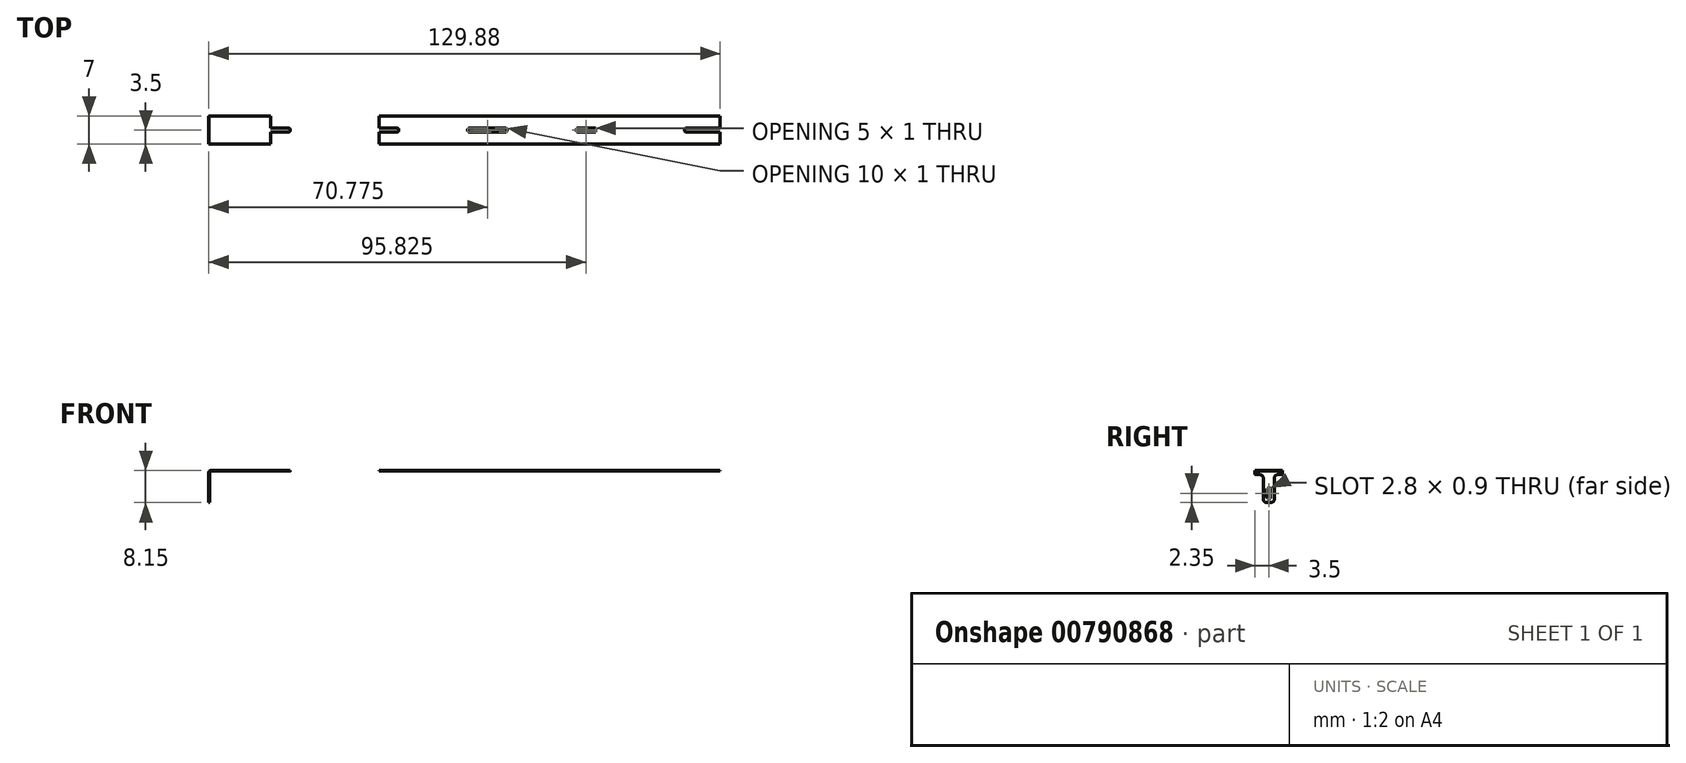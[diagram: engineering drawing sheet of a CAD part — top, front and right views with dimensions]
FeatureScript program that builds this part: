
annotation { "Feature Type Name" : "Feature", "Feature Type Description" : "" }
export const myFeature = defineFeature(function(context is Context, id is Id, definition is map)
    precondition{}
    {
        {
            var Q0;
            Q0=qCreatedBy(makeId("Top.planeOp"),FACE);
            var sketch = newSketch(context, id + "F0", { "sketchPlane" : qUnion([Q0])});
            skPoint(sketch, "E0.middle", {"position": v(0, 0) * mm});
            skLineSegment(sketch, "E1.bottom", {"start": v(-9.18, -0.5) * mm, "end": v(-13.77, -0.5) * mm});
            skLineSegment(sketch, "E1.top", {"start": v(-9.18, 0.5) * mm, "end": v(-13.77, 0.5) * mm});
            skLineSegment(sketch, "E1.left", {"start": v(-8.78, -0.1) * mm, "end": v(-8.78, 0.1) * mm});
            skLineSegment(sketch, "E1.right", {"start": v(-18.78, -0.1) * mm, "end": v(-18.78, 0.1) * mm});
            skPoint(sketch, "E1.middle", {"position": v(-13.78, 0) * mm});
            skPoint(sketch, "E2.visualSharp", {"position": v(-8.78, 0.5) * mm});
            skArc(sketch, "E2.filletArc", {"start": v(-8.78, 0.1) * mm, "mid": v(-8.9, 0.38) * mm, "end": v(-9.18, 0.5) * mm});
            skPoint(sketch, "E3.visualSharp", {"position": v(-8.78, -0.5) * mm});
            skArc(sketch, "E3.filletArc", {"start": v(-9.18, -0.5) * mm, "mid": v(-8.9, -0.38) * mm, "end": v(-8.78, -0.1) * mm});
            skPoint(sketch, "E4.visualSharp", {"position": v(-18.78, 0.5) * mm});
            skArc(sketch, "E4.filletArc", {"start": v(-18.38, 0.5) * mm, "mid": v(-18.66, 0.38) * mm, "end": v(-18.77, 0.1) * mm});
            skPoint(sketch, "E5.visualSharp", {"position": v(-18.78, -0.5) * mm});
            skArc(sketch, "E5.filletArc", {"start": v(-18.77, -0.1) * mm, "mid": v(-18.66, -0.38) * mm, "end": v(-18.38, -0.5) * mm});
            skLineSegment(sketch, "E6", {"start": v(0, 3.5) * mm, "end": v(-13.78, 3.5) * mm});
            skPoint(sketch, "E6.endSnap0", {"position": v(-13.77, 0.5) * mm});
            skLineSegment(sketch, "E7", {"start": v(-13.78, 3.5) * mm, "end": v(-13.78, 0.5) * mm});
            skLineSegment(sketch, "E8.MirrorCS", {"start": v(0, -3.5) * mm, "end": v(-13.78, -3.5) * mm});
            skLineSegment(sketch, "E9.MirrorCS", {"start": v(-13.78, -3.5) * mm, "end": v(-13.78, -0.5) * mm});
            skLineSegment(sketch, "E10.MirrorCS", {"start": v(0, 3.5) * mm, "end": v(13.78, 3.5) * mm});
            skLineSegment(sketch, "E11.MirrorCS", {"start": v(0, -3.5) * mm, "end": v(13.78, -3.5) * mm});
            skLineSegment(sketch, "E12.MirrorCS", {"start": v(8.78, -0.1) * mm, "end": v(8.78, 0.1) * mm});
            skArc(sketch, "E13.MirrorCS", {"start": v(8.78, 0.1) * mm, "mid": v(8.9, 0.38) * mm, "end": v(9.18, 0.5) * mm});
            skArc(sketch, "E14.MirrorCS", {"start": v(18.77, -0.1) * mm, "mid": v(18.66, -0.38) * mm, "end": v(18.38, -0.5) * mm});
            skLineSegment(sketch, "E15.MirrorCS", {"start": v(18.78, -0.1) * mm, "end": v(18.78, 0.1) * mm});
            skArc(sketch, "E16.MirrorCS", {"start": v(18.38, 0.5) * mm, "mid": v(18.66, 0.38) * mm, "end": v(18.77, 0.1) * mm});
            skArc(sketch, "E17.MirrorCS", {"start": v(9.18, -0.5) * mm, "mid": v(8.9, -0.38) * mm, "end": v(8.78, -0.1) * mm});
            skPoint(sketch, "E18.MirrorP", {"position": v(18.78, 0.5) * mm});
            skLineSegment(sketch, "E19.MirrorCS", {"start": v(9.18, 0.5) * mm, "end": v(18.38, 0.5) * mm});
            skLineSegment(sketch, "E20.MirrorCS", {"start": v(9.18, -0.5) * mm, "end": v(18.38, -0.5) * mm});
            skPoint(sketch, "E21.MirrorP", {"position": v(13.77, 0.5) * mm});
            skPoint(sketch, "E22.MirrorP", {"position": v(8.78, 0.5) * mm});
            skPoint(sketch, "E23.MirrorP", {"position": v(18.78, -0.5) * mm});
            skPoint(sketch, "E24.MirrorP", {"position": v(8.78, -0.5) * mm});
            skPoint(sketch, "E25.MirrorP", {"position": v(13.78, 0) * mm});
            skLineSegment(sketch, "E26.MirrorCS", {"start": v(13.78, 3.5) * mm, "end": v(13.78, 0.5) * mm});
            skLineSegment(sketch, "E27.MirrorCS", {"start": v(13.78, -3.5) * mm, "end": v(13.78, -0.5) * mm});
            skPoint(sketch, "E28.1.0.0", {"position": v(36.33, 0.5) * mm});
            skLineSegment(sketch, "E28.1.0.1", {"start": v(27.55, 3.5) * mm, "end": v(41.33, 3.5) * mm});
            skLineSegment(sketch, "E28.1.0.2", {"start": v(36.73, -0.5) * mm, "end": v(45.93, -0.5) * mm});
            skPoint(sketch, "E28.1.0.3", {"position": v(27.55, 0) * mm});
            skLineSegment(sketch, "E28.1.0.4", {"start": v(27.55, -3.5) * mm, "end": v(41.33, -3.5) * mm});
            skPoint(sketch, "E28.1.0.5", {"position": v(41.33, 0.5) * mm});
            skPoint(sketch, "E28.1.0.6", {"position": v(41.33, 0) * mm});
            skPoint(sketch, "E28.1.0.7", {"position": v(46.33, -0.5) * mm});
            skPoint(sketch, "E28.1.0.8", {"position": v(36.33, -0.5) * mm});
            skLineSegment(sketch, "E28.1.0.9", {"start": v(27.55, -3.5) * mm, "end": v(13.78, -3.5) * mm});
            skLineSegment(sketch, "E28.1.0.10", {"start": v(36.73, 0.5) * mm, "end": v(45.93, 0.5) * mm});
            skLineSegment(sketch, "E28.1.0.11", {"start": v(27.55, 3.5) * mm, "end": v(13.78, 3.5) * mm});
            skLineSegment(sketch, "E28.1.0.12", {"start": v(41.33, 3.5) * mm, "end": v(41.33, 0.5) * mm});
            skLineSegment(sketch, "E28.1.0.13", {"start": v(41.33, -3.5) * mm, "end": v(41.33, -0.5) * mm});
            skPoint(sketch, "E28.1.0.14", {"position": v(46.33, 0.5) * mm});
            skArc(sketch, "E28.1.0.15", {"start": v(45.93, 0.5) * mm, "mid": v(46.2, 0.38) * mm, "end": v(46.32, 0.1) * mm});
            skArc(sketch, "E28.1.0.16", {"start": v(36.73, -0.5) * mm, "mid": v(36.44, -0.38) * mm, "end": v(36.33, -0.1) * mm});
            skArc(sketch, "E28.1.0.17", {"start": v(46.33, -0.1) * mm, "mid": v(46.2, -0.38) * mm, "end": v(45.93, -0.5) * mm});
            skArc(sketch, "E28.1.0.18", {"start": v(36.33, 0.1) * mm, "mid": v(36.44, 0.38) * mm, "end": v(36.73, 0.5) * mm});
            skLineSegment(sketch, "E28.1.0.19", {"start": v(36.32, -0.1) * mm, "end": v(36.32, 0.1) * mm});
            skLineSegment(sketch, "E28.1.0.20", {"start": v(46.33, -0.1) * mm, "end": v(46.33, 0.1) * mm});
            skPoint(sketch, "E28.2.0.0", {"position": v(63.88, 0.5) * mm});
            skLineSegment(sketch, "E28.2.0.1", {"start": v(55.1, 3.5) * mm, "end": v(68.88, 3.5) * mm});
            skLineSegment(sketch, "E28.2.0.2", {"start": v(64.28, -0.5) * mm, "end": v(73.48, -0.5) * mm});
            skPoint(sketch, "E28.2.0.3", {"position": v(55.1, 0) * mm});
            skLineSegment(sketch, "E28.2.0.4", {"start": v(55.1, -3.5) * mm, "end": v(68.88, -3.5) * mm});
            skPoint(sketch, "E28.2.0.5", {"position": v(68.88, 0.5) * mm});
            skPoint(sketch, "E28.2.0.6", {"position": v(68.88, 0) * mm});
            skPoint(sketch, "E28.2.0.7", {"position": v(73.88, -0.5) * mm});
            skPoint(sketch, "E28.2.0.8", {"position": v(63.88, -0.5) * mm});
            skLineSegment(sketch, "E28.2.0.9", {"start": v(55.1, -3.5) * mm, "end": v(41.33, -3.5) * mm});
            skLineSegment(sketch, "E28.2.0.10", {"start": v(64.28, 0.5) * mm, "end": v(73.48, 0.5) * mm});
            skLineSegment(sketch, "E28.2.0.11", {"start": v(55.1, 3.5) * mm, "end": v(41.33, 3.5) * mm});
            skLineSegment(sketch, "E28.2.0.12", {"start": v(68.88, 3.5) * mm, "end": v(68.88, 0.5) * mm});
            skLineSegment(sketch, "E28.2.0.13", {"start": v(68.88, -3.5) * mm, "end": v(68.88, -0.5) * mm});
            skPoint(sketch, "E28.2.0.14", {"position": v(73.88, 0.5) * mm});
            skArc(sketch, "E28.2.0.15", {"start": v(73.48, 0.5) * mm, "mid": v(73.76, 0.38) * mm, "end": v(73.88, 0.1) * mm});
            skArc(sketch, "E28.2.0.16", {"start": v(64.28, -0.5) * mm, "mid": v(64, -0.38) * mm, "end": v(63.88, -0.1) * mm});
            skArc(sketch, "E28.2.0.17", {"start": v(73.88, -0.1) * mm, "mid": v(73.76, -0.38) * mm, "end": v(73.48, -0.5) * mm});
            skArc(sketch, "E28.2.0.18", {"start": v(63.88, 0.1) * mm, "mid": v(64, 0.38) * mm, "end": v(64.28, 0.5) * mm});
            skLineSegment(sketch, "E28.2.0.19", {"start": v(63.88, -0.1) * mm, "end": v(63.88, 0.1) * mm});
            skLineSegment(sketch, "E28.2.0.20", {"start": v(73.88, -0.1) * mm, "end": v(73.88, 0.1) * mm});
            skPoint(sketch, "E28.3.0.0", {"position": v(91.43, 0.5) * mm});
            skLineSegment(sketch, "E28.3.0.1", {"start": v(82.65, 3.5) * mm, "end": v(96.43, 3.5) * mm});
            skLineSegment(sketch, "E28.3.0.2", {"start": v(91.83, -0.5) * mm, "end": v(101.03, -0.5) * mm});
            skPoint(sketch, "E28.3.0.3", {"position": v(82.65, 0) * mm});
            skLineSegment(sketch, "E28.3.0.4", {"start": v(82.65, -3.5) * mm, "end": v(96.43, -3.5) * mm});
            skPoint(sketch, "E28.3.0.5", {"position": v(96.43, 0.5) * mm});
            skPoint(sketch, "E28.3.0.6", {"position": v(96.42, 0) * mm});
            skPoint(sketch, "E28.3.0.7", {"position": v(101.42, -0.5) * mm});
            skPoint(sketch, "E28.3.0.8", {"position": v(91.43, -0.5) * mm});
            skLineSegment(sketch, "E28.3.0.9", {"start": v(82.65, -3.5) * mm, "end": v(68.88, -3.5) * mm});
            skLineSegment(sketch, "E28.3.0.10", {"start": v(91.83, 0.5) * mm, "end": v(101.03, 0.5) * mm});
            skLineSegment(sketch, "E28.3.0.11", {"start": v(82.65, 3.5) * mm, "end": v(68.88, 3.5) * mm});
            skLineSegment(sketch, "E28.3.0.12", {"start": v(96.43, 3.5) * mm, "end": v(96.43, 0.5) * mm});
            skLineSegment(sketch, "E28.3.0.13", {"start": v(96.43, -3.5) * mm, "end": v(96.43, -0.5) * mm});
            skPoint(sketch, "E28.3.0.14", {"position": v(101.42, 0.5) * mm});
            skArc(sketch, "E28.3.0.15", {"start": v(101.03, 0.5) * mm, "mid": v(101.3, 0.38) * mm, "end": v(101.42, 0.1) * mm});
            skArc(sketch, "E28.3.0.16", {"start": v(91.83, -0.5) * mm, "mid": v(91.54, -0.38) * mm, "end": v(91.43, -0.1) * mm});
            skArc(sketch, "E28.3.0.17", {"start": v(101.42, -0.1) * mm, "mid": v(101.3, -0.38) * mm, "end": v(101.03, -0.5) * mm});
            skArc(sketch, "E28.3.0.18", {"start": v(91.43, 0.1) * mm, "mid": v(91.54, 0.38) * mm, "end": v(91.83, 0.5) * mm});
            skLineSegment(sketch, "E28.3.0.19", {"start": v(91.43, -0.1) * mm, "end": v(91.43, 0.1) * mm});
            skLineSegment(sketch, "E28.3.0.20", {"start": v(101.42, -0.1) * mm, "end": v(101.42, 0.1) * mm});
            skLineSegment(sketch, "E28.direction1", {"start": v(-13.78, -3.5) * mm, "end": v(13.78, -3.5) * mm, "construction": true});
            skLineSegment(sketch, "E29", {"start": v(0, 3.5) * mm, "end": v(0, -3.5) * mm});
            skLineSegment(sketch, "E30.bottom", {"start": v(96.43, -3.5) * mm, "end": v(100.42, -3.5) * mm});
            skLineSegment(sketch, "E30.top", {"start": v(96.43, 3.5) * mm, "end": v(100.42, 3.5) * mm});
            skLineSegment(sketch, "E30.left", {"start": v(96.43, -3.5) * mm, "end": v(96.43, 3.5) * mm});
            skPoint(sketch, "E31.0.4.0", {"position": v(118.98, 0.5) * mm});
            skLineSegment(sketch, "E31.1.4.0", {"start": v(110.2, 3.5) * mm, "end": v(123.98, 3.5) * mm});
            skLineSegment(sketch, "E31.4.4.0", {"start": v(119.38, -0.5) * mm, "end": v(128.57, -0.5) * mm});
            skPoint(sketch, "E31.7.4.0", {"position": v(110.2, 0) * mm});
            skLineSegment(sketch, "E31.8.4.0", {"start": v(110.2, -3.5) * mm, "end": v(123.98, -3.5) * mm});
            skPoint(sketch, "E31.11.4.0", {"position": v(123.98, 0.5) * mm});
            skPoint(sketch, "E31.12.4.0", {"position": v(123.98, 0) * mm});
            skPoint(sketch, "E31.13.4.0", {"position": v(128.97, -0.5) * mm});
            skPoint(sketch, "E31.14.4.0", {"position": v(118.98, -0.5) * mm});
            skLineSegment(sketch, "E31.15.4.0", {"start": v(110.2, -3.5) * mm, "end": v(96.43, -3.5) * mm});
            skLineSegment(sketch, "E31.18.4.0", {"start": v(119.38, 0.5) * mm, "end": v(128.57, 0.5) * mm});
            skLineSegment(sketch, "E31.21.4.0", {"start": v(110.2, 3.5) * mm, "end": v(96.43, 3.5) * mm});
            skLineSegment(sketch, "E31.24.4.0", {"start": v(123.98, 3.5) * mm, "end": v(123.98, 0.5) * mm});
            skLineSegment(sketch, "E31.27.4.0", {"start": v(123.98, -3.5) * mm, "end": v(123.98, -0.5) * mm});
            skPoint(sketch, "E31.30.4.0", {"position": v(128.97, 0.5) * mm});
            skArc(sketch, "E31.31.4.0", {"start": v(128.57, 0.5) * mm, "mid": v(128.86, 0.38) * mm, "end": v(128.97, 0.1) * mm});
            skArc(sketch, "E31.35.4.0", {"start": v(119.38, -0.5) * mm, "mid": v(119.1, -0.38) * mm, "end": v(118.98, -0.1) * mm});
            skArc(sketch, "E31.39.4.0", {"start": v(128.97, -0.1) * mm, "mid": v(128.86, -0.38) * mm, "end": v(128.57, -0.5) * mm});
            skArc(sketch, "E31.43.4.0", {"start": v(118.98, 0.1) * mm, "mid": v(119.1, 0.38) * mm, "end": v(119.38, 0.5) * mm});
            skLineSegment(sketch, "E31.47.4.0", {"start": v(118.98, -0.1) * mm, "end": v(118.98, 0.1) * mm});
            skLineSegment(sketch, "E31.50.4.0", {"start": v(128.97, -0.1) * mm, "end": v(128.97, 0.1) * mm});
            skLineSegment(sketch, "E32.bottom", {"start": v(123.98, -3.5) * mm, "end": v(127.98, -3.5) * mm});
            skLineSegment(sketch, "E32.top", {"start": v(123.98, 3.5) * mm, "end": v(127.98, 3.5) * mm});
            skLineSegment(sketch, "E32.left", {"start": v(123.98, -3.5) * mm, "end": v(123.98, 3.5) * mm});
            skLineSegment(sketch, "E32.right", {"start": v(127.98, -3.5) * mm, "end": v(127.98, 3.5) * mm});
            skSolve(sketch);
        }
        {
            var Q0;
            {var subQ8=sQuery(id+"F0.wireOp",EDGE,"E28.3.0.12");Q0=makeQuery(id+"F0.imprint","IMPRINT",FACE,{"disambiguationData":[TD([[makeQuery(id+"F0.imprint","IMPRINT",EDGE,{"derivedFrom":subQ8}),1.0]])]});}
            var Q1;
            {var subQ3=sQuery(id+"F0.wireOp",EDGE,"E14.MirrorCS");Q1=makeQuery(id+"F0.imprint","IMPRINT",FACE,{"disambiguationData":[TD([[makeQuery(id+"F0.imprint","IMPRINT",EDGE,{"derivedFrom":subQ3}),1.0]])]});}
            var Q2;
            {var subQ8=sQuery(id+"F0.wireOp",EDGE,"E28.1.0.12");Q2=makeQuery(id+"F0.imprint","IMPRINT",FACE,{"disambiguationData":[TD([[makeQuery(id+"F0.imprint","IMPRINT",EDGE,{"derivedFrom":subQ8}),1.0]])]});}
            var Q3;
            {var subQ8=sQuery(id+"F0.wireOp",EDGE,"E28.2.0.12");Q3=makeQuery(id+"F0.imprint","IMPRINT",FACE,{"disambiguationData":[TD([[makeQuery(id+"F0.imprint","IMPRINT",EDGE,{"derivedFrom":subQ8}),1.0]])]});}
            var Q4;
            Q4=makeQuery(id+"F0.imprint","IMPRINT",FACE,{"disambiguationData":[TD([[makeQuery(id+"F0.imprint","IMPRINT",EDGE,{"derivedFrom":sQuery(id+"F0.wireOp",EDGE,"E10.MirrorCS")}),-1.0]])]});
            var Q5;
            {var subQ5=sQuery(id+"F0.wireOp",EDGE,"E30.top");Q5=makeQuery(id+"F0.imprint","IMPRINT",FACE,{"disambiguationData":[TD([[makeQuery(id+"F0.imprint","IMPRINT",EDGE,{"derivedFrom":subQ5}),-1.0]])]});}
            var Q6;
            {var subQ5=sQuery(id+"F0.wireOp",EDGE,"E30.bottom");Q6=makeQuery(id+"F0.imprint","IMPRINT",FACE,{"disambiguationData":[TD([[makeQuery(id+"F0.imprint","IMPRINT",EDGE,{"derivedFrom":subQ5}),1.0]])]});}
            var Q7;
            {var subQ11=sQuery(id+"F0.wireOp",EDGE,"E28.3.0.15");Q7=makeQuery(id+"F0.imprint","IMPRINT",FACE,{"disambiguationData":[TD([[makeQuery(id+"F0.imprint","IMPRINT",EDGE,{"derivedFrom":subQ11}),1.0]])]});}
            var Q8;
            {var subQ5=sQuery(id+"F0.wireOp",EDGE,"E32.bottom");Q8=makeQuery(id+"F0.imprint","IMPRINT",FACE,{"disambiguationData":[TD([[makeQuery(id+"F0.imprint","IMPRINT",EDGE,{"derivedFrom":subQ5}),1.0]])]});}
            var Q9;
            {var subQ5=sQuery(id+"F0.wireOp",EDGE,"E32.top");Q9=makeQuery(id+"F0.imprint","IMPRINT",FACE,{"disambiguationData":[TD([[makeQuery(id+"F0.imprint","IMPRINT",EDGE,{"derivedFrom":subQ5}),-1.0]])]});}
            extrude(context, id + "F1", {"entities" : qUnion([Q0, Q1, Q2, Q3, Q4, Q5, Q6, Q7, Q8, Q9]), "depth" : 0.15 * mm, "offsetDistance" : 25 * mm});
        }
        {
            var Q0;
            Q0=makeQuery(id+"F1.opExtrude","SWEPT_FACE",FACE,{"disambiguationData":[OSD([sQuery(id+"F0.wireOp",EDGE,"E29")])]});
            extrude(context, id + "F2", {"entities" : qUnion([Q0]), "operationType" : NewBodyOperationType.ADD, "depth" : 1.9 * mm, "offsetDistance" : 25 * mm});
        }
        {
            var Q0;
            {var subQ0=sQuery(id+"F0.wireOp",EDGE,"E29");Q0=makeQuery(id+"F2.boolean.opBoolean","MERGE",FACE,{"derivedFrom":[makeQuery(id+"F1.opExtrude","CAP_FACE",FACE,{"disambiguationData":[OSD([sQuery(id+"F0.wireOp",EDGE,"E10.MirrorCS"),sQuery(id+"F0.wireOp",EDGE,"E11.MirrorCS"),sQuery(id+"F0.wireOp",EDGE,"E12.MirrorCS"),sQuery(id+"F0.wireOp",EDGE,"E13.MirrorCS"),sQuery(id+"F0.wireOp",EDGE,"E14.MirrorCS"),sQuery(id+"F0.wireOp",EDGE,"E15.MirrorCS"),sQuery(id+"F0.wireOp",EDGE,"E16.MirrorCS"),sQuery(id+"F0.wireOp",EDGE,"E17.MirrorCS"),sQuery(id+"F0.wireOp",EDGE,"E19.MirrorCS"),sQuery(id+"F0.wireOp",EDGE,"E20.MirrorCS"),sQuery(id+"F0.wireOp",EDGE,"E28.1.0.1"),sQuery(id+"F0.wireOp",EDGE,"E28.1.0.2"),sQuery(id+"F0.wireOp",EDGE,"E28.1.0.4"),sQuery(id+"F0.wireOp",EDGE,"E28.1.0.9"),sQuery(id+"F0.wireOp",EDGE,"E28.1.0.10"),sQuery(id+"F0.wireOp",EDGE,"E28.1.0.11"),sQuery(id+"F0.wireOp",EDGE,"E28.1.0.15"),sQuery(id+"F0.wireOp",EDGE,"E28.1.0.16"),sQuery(id+"F0.wireOp",EDGE,"E28.1.0.17"),sQuery(id+"F0.wireOp",EDGE,"E28.1.0.18"),sQuery(id+"F0.wireOp",EDGE,"E28.1.0.19"),sQuery(id+"F0.wireOp",EDGE,"E28.1.0.20"),sQuery(id+"F0.wireOp",EDGE,"E28.2.0.1"),sQuery(id+"F0.wireOp",EDGE,"E28.2.0.2"),sQuery(id+"F0.wireOp",EDGE,"E28.2.0.4"),sQuery(id+"F0.wireOp",EDGE,"E28.2.0.9"),sQuery(id+"F0.wireOp",EDGE,"E28.2.0.10"),sQuery(id+"F0.wireOp",EDGE,"E28.2.0.11"),sQuery(id+"F0.wireOp",EDGE,"E28.2.0.15"),sQuery(id+"F0.wireOp",EDGE,"E28.2.0.16"),sQuery(id+"F0.wireOp",EDGE,"E28.2.0.17"),sQuery(id+"F0.wireOp",EDGE,"E28.2.0.18"),sQuery(id+"F0.wireOp",EDGE,"E28.2.0.19"),sQuery(id+"F0.wireOp",EDGE,"E28.2.0.20"),sQuery(id+"F0.wireOp",EDGE,"E28.3.0.1"),sQuery(id+"F0.wireOp",EDGE,"E28.3.0.2"),sQuery(id+"F0.wireOp",EDGE,"E28.3.0.4"),sQuery(id+"F0.wireOp",EDGE,"E28.3.0.9"),sQuery(id+"F0.wireOp",EDGE,"E28.3.0.10"),sQuery(id+"F0.wireOp",EDGE,"E28.3.0.11"),sQuery(id+"F0.wireOp",EDGE,"E28.3.0.12"),sQuery(id+"F0.wireOp",EDGE,"E28.3.0.13"),sQuery(id+"F0.wireOp",EDGE,"E28.3.0.16"),sQuery(id+"F0.wireOp",EDGE,"E28.3.0.18"),sQuery(id+"F0.wireOp",EDGE,"E28.3.0.19"),subQ0])],"isStart":true}),makeQuery(id+"F2.opExtrude","SWEPT_FACE",FACE,{"disambiguationData":[OSD([subQ0]),TDD([makeQuery(id+"F1.opExtrude","CAP_EDGE",EDGE,{"disambiguationData":[OSD([subQ0])],"isStart":true})])]})]});}
            var sketch = newSketch(context, id + "F3", { "sketchPlane" : qUnion([Q0])});
            skLineSegment(sketch, "E33.bottom", {"start": v(-1.9, -3.5) * mm, "end": v(-1.75, -3.5) * mm});
            skLineSegment(sketch, "E33.top", {"start": v(-1.9, 3.5) * mm, "end": v(-1.75, 3.5) * mm});
            skLineSegment(sketch, "E33.left", {"start": v(-1.9, -3.5) * mm, "end": v(-1.9, 3.5) * mm});
            skLineSegment(sketch, "E33.right", {"start": v(-1.75, -3.5) * mm, "end": v(-1.75, 3.5) * mm});
            skSolve(sketch);
        }
        {
            var Q0;
            Q0=qSketchRegion(id+"F3",true);
            extrude(context, id + "F4", {"entities" : qUnion([Q0]), "operationType" : NewBodyOperationType.ADD, "depth" : 8 * mm, "offsetDistance" : 25 * mm});
        }
        {
            var Q0;
            Q0=makeQuery(id+"F4.boolean.opBoolean","MERGE",FACE,{"derivedFrom":[makeQuery(id+"F2.opExtrude","CAP_FACE",FACE,{"disambiguationData":[OSD([sQuery(id+"F0.wireOp",EDGE,"E29")])],"isStart":false}),makeQuery(id+"F4.opExtrude","SWEPT_FACE",FACE,{"disambiguationData":[OSD([sQuery(id+"F3.wireOp",EDGE,"E33.left")])]})]});
            var sketch = newSketch(context, id + "F5", { "sketchPlane" : qUnion([Q0])});
            skLineSegment(sketch, "E34.bottom", {"start": v(-0.5, -8) * mm, "end": v(0.5, -8) * mm});
            skLineSegment(sketch, "E34.top", {"start": v(-1.4, -0.9) * mm, "end": v(1.4, -0.9) * mm});
            skLineSegment(sketch, "E34.left", {"start": v(-1.4, -7.1) * mm, "end": v(-1.4, -1.8) * mm});
            skLineSegment(sketch, "E34.right", {"start": v(1.4, -7.1) * mm, "end": v(1.4, -1.8) * mm});
            skLineSegment(sketch, "E35", {"start": v(2.3, -0.9) * mm, "end": v(3.4, -0.9) * mm});
            skLineSegment(sketch, "E36", {"start": v(-2.3, -0.9) * mm, "end": v(-3.4, -0.9) * mm});
            skCircle(sketch, "E37", {"center": v(0, -6.6) * mm, "radius": 0.45 * mm});
            skCircle(sketch, "E38", {"center": v(0, -4.7) * mm, "radius": 0.45 * mm});
            skLineSegment(sketch, "E39", {"start": v(0.45, -4.7) * mm, "end": v(0.45, -6.6) * mm});
            skLineSegment(sketch, "E40", {"start": v(-0.45, -4.7) * mm, "end": v(-0.45, -6.6) * mm});
            skPoint(sketch, "E41.visualSharp", {"position": v(-1.4, -8) * mm});
            skArc(sketch, "E41.filletArc", {"start": v(-1.4, -7.1) * mm, "mid": v(-1.14, -7.74) * mm, "end": v(-0.5, -8) * mm});
            skPoint(sketch, "E42.visualSharp", {"position": v(1.4, -8) * mm});
            skArc(sketch, "E42.filletArc", {"start": v(0.5, -8) * mm, "mid": v(1.14, -7.74) * mm, "end": v(1.4, -7.1) * mm});
            skPoint(sketch, "E43.visualSharp", {"position": v(-1.4, -0.9) * mm});
            skArc(sketch, "E43.filletArc", {"start": v(-1.4, -1.8) * mm, "mid": v(-1.66, -1.16) * mm, "end": v(-2.3, -0.9) * mm});
            skPoint(sketch, "E44.visualSharp", {"position": v(1.4, -0.9) * mm});
            skArc(sketch, "E44.filletArc", {"start": v(2.3, -0.9) * mm, "mid": v(1.66, -1.16) * mm, "end": v(1.4, -1.8) * mm});
            skLineSegment(sketch, "E45", {"start": v(-3.5, -0.8) * mm, "end": v(-3.5, 0.15) * mm});
            skLineSegment(sketch, "E46", {"start": v(3.5, -0.8) * mm, "end": v(3.5, 0.15) * mm});
            skPoint(sketch, "E47.visualSharp", {"position": v(-3.5, -0.9) * mm});
            skArc(sketch, "E47.filletArc", {"start": v(-3.5, -0.8) * mm, "mid": v(-3.47, -0.87) * mm, "end": v(-3.4, -0.9) * mm});
            skPoint(sketch, "E48.visualSharp", {"position": v(3.5, -0.9) * mm});
            skArc(sketch, "E48.filletArc", {"start": v(3.4, -0.9) * mm, "mid": v(3.47, -0.87) * mm, "end": v(3.5, -0.8) * mm});
            skSolve(sketch);
        }
        {
            var Q0;
            Q0=makeQuery(id+"F5.imprint","IMPRINT",FACE,{"disambiguationData":[TD([[makeQuery(id+"F5.imprint","IMPRINT",EDGE,{"derivedFrom":sQuery(id+"F5.wireOp",EDGE,"E34.right")}),-1.0]])]});
            var Q1;
            Q1=makeQuery(id+"F5.imprint","IMPRINT",FACE,{"disambiguationData":[TD([[makeQuery(id+"F5.imprint","IMPRINT",EDGE,{"derivedFrom":sQuery(id+"F5.wireOp",EDGE,"E34.left")}),1.0]])]});
            var Q2;
            {var subQ0=sQuery(id+"F5.wireOp",EDGE,"E38");var subQ1=makeQuery(id+"F5.imprint","INTERSECT",VERTEX,{"derivedFrom":[subQ0,sQuery(id+"F5.wireOp",EDGE,"E39")]});Q2=makeQuery(id+"F5.imprint","IMPRINT",FACE,{"disambiguationData":[TD([[makeQuery(id+"F5.imprint","IMPRINT",EDGE,{"disambiguationData":[TD([[subQ1,-1.0]])],"derivedFrom":subQ0}),1.0]])]});}
            var Q3;
            {var subQ0=sQuery(id+"F5.wireOp",EDGE,"E39");Q3=makeQuery(id+"F5.imprint","IMPRINT",FACE,{"disambiguationData":[TD([[makeQuery(id+"F5.imprint","IMPRINT",EDGE,{"derivedFrom":subQ0}),-1.0]])]});}
            var Q4;
            {var subQ0=sQuery(id+"F5.wireOp",EDGE,"E37");var subQ1=makeQuery(id+"F5.imprint","INTERSECT",VERTEX,{"derivedFrom":[subQ0,sQuery(id+"F5.wireOp",EDGE,"E39")]});Q4=makeQuery(id+"F5.imprint","IMPRINT",FACE,{"disambiguationData":[TD([[makeQuery(id+"F5.imprint","IMPRINT",EDGE,{"disambiguationData":[TD([[subQ1,-1.0]])],"derivedFrom":subQ0}),1.0]])]});}
            extrude(context, id + "F6", {"entities" : qUnion([Q0, Q1, Q2, Q3, Q4]), "operationType" : NewBodyOperationType.REMOVE, "oppositeDirection" : true, "depth" : 25 * mm, "offsetDistance" : 25 * mm});
        }
        {
            var Q0;
            {var subQ0=sQuery(id+"F0.wireOp",EDGE,"E29");Q0=makeQuery(id+"F2.opExtrude","CAP_EDGE",EDGE,{"disambiguationData":[OSD([subQ0]),TDD([makeQuery(id+"F1.opExtrude","CAP_EDGE",EDGE,{"disambiguationData":[OSD([subQ0])],"isStart":false})])],"isStart":false});}
            var Q1;
            Q1=makeQuery(id+"F4.opExtrude","CAP_EDGE",EDGE,{"disambiguationData":[OSD([sQuery(id+"F3.wireOp",EDGE,"E33.right")])],"isStart":true});
            fillet(context, id + "F7", {"entities" : qUnion([Q0, Q1]), "radius" : 0.5 * mm, "tangentPropagation" : true, "allowEdgeOverflow" : false});
        }
    });
